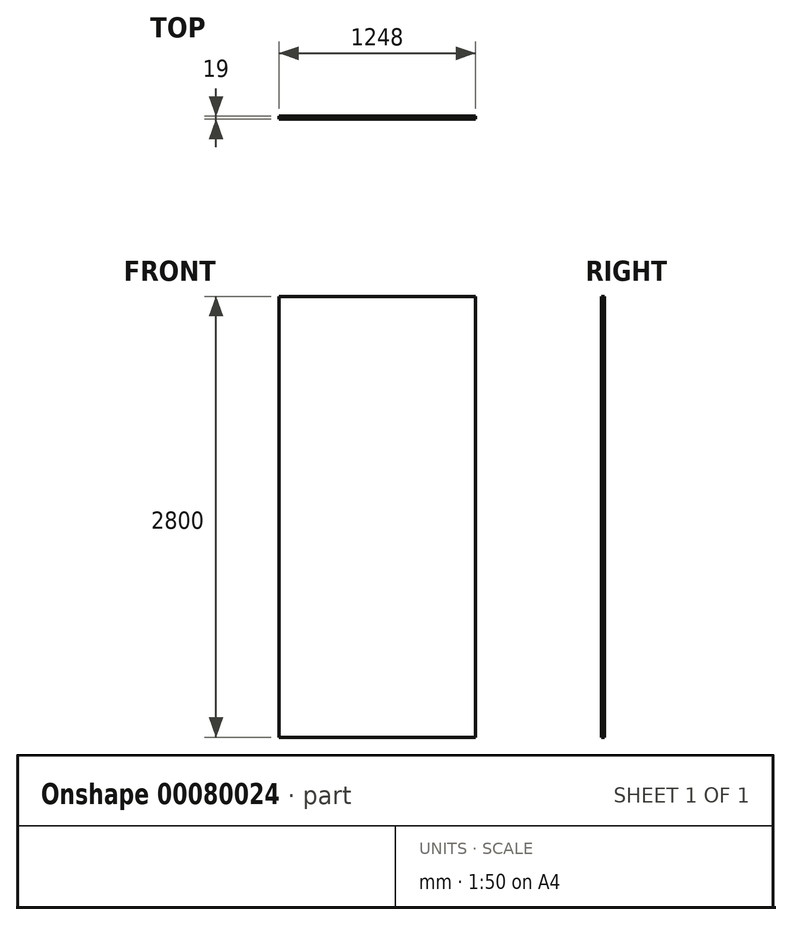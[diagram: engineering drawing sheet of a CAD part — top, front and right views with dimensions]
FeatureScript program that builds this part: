
annotation { "Feature Type Name" : "Feature", "Feature Type Description" : "" }
export const myFeature = defineFeature(function(context is Context, id is Id, definition is map)
    precondition{}
    {
        {
            var Q0;
            Q0=qCreatedBy(makeId("Front.planeOp"),FACE);
            var sketch = newSketch(context, id + "F0", { "sketchPlane" : qUnion([Q0])});
            skLineSegment(sketch, "E0.bottom", {"start": v(0, 0) * mm, "end": v(1248, 0) * mm});
            skLineSegment(sketch, "E0.top", {"start": v(0, -2800) * mm, "end": v(1248, -2800) * mm});
            skLineSegment(sketch, "E0.left", {"start": v(0, 0) * mm, "end": v(0, -2800) * mm});
            skLineSegment(sketch, "E0.right", {"start": v(1248, 0) * mm, "end": v(1248, -2800) * mm});
            skSolve(sketch);
        }
        {
            var Q0;
            Q0 = qSketchRegion(id + "F0", true);
            extrude(context, id + "F1", {"entities" : qUnion([Q0]), "depth" : 19 * mm});
        }
    });
